# Revit family: RK-ZONE8
name_source: partatom
category: Electrical Equipment
revit_build: Autodesk Revit 2016 (Build: 20150220_1215(x64)
units: mm (PartAtom-declared; Revit-internal decimal feet)

## family parameters
Always vertical = Yes
Cut with Voids When Loaded = No
OmniClass Number = 23.80.30.11.17
OmniClass Title = Distribution Boards and Control Panels
Panel Configuration = Two Columns, Circuits Across
Part Type = Panelboard
Room Calculation Point = No
Round Connector Dimension = Use Diameter
Shared = No
Work Plane-Based = No

## types (1)
- RK-ZONE8
    Access Clearance Bottom = 0 mm  [stored 0 ft]
    Access Clearance Front = 0 mm  [stored 0 ft]
    Access Clearance Left = 0 mm  [stored 0 ft]
    Access Clearance Rear = 0 mm  [stored 0 ft]
    Access Clearance Right = 0 mm  [stored 0 ft]
    Access Clearance Top = 0 mm  [stored 0 ft]
    BMS Links = Yes
    Battery Type = e.g. Alkaline, Lithium Ion Rechargeable
    CE Approval = Number, Yes, No
    Coverage Area = 0.06 m²
    Default elevation = 1219 mm
    Embodied Carbon = kgCO2
    Enclosure Rating = IP rating
    Energy Technology List = External data hyperconnection
    Environmental Product Declaration = 3rd Party Verification
    Expected Life = *Years
    Features = Free text to describe product
    Fire Control Panel Links = Yes
    Frequency = 350 Hz ~ 12 kHz
    Green Guide for Specification = A - E
    Gross Weight = 2.05Kg
    Life Cycle Analysis = A - E
    Location of Manufacturer = Northing,Easting
    Manufacturer Website = External data hyperconnection
    Material = Steel
    Material2 = cutout
    Number of Poles = 3
    O&M Manual = External data hyperconnection
    Overall Height = 165 mm
    Overall Length = 240 mm  [stored 0.787402 ft]
    Overall Width = 225 mm  [stored 0.738189 ft]
    Product Model Number = Or  Code
    Responsible Sourcing of Materials = Endorsing body
    Set Point Concentration = 0 m²
    Supply Phase = 3
    voltage = 100V/70V

note: [stored X ft] marks values corroborated as IEEE doubles in the binary element streams (Revit-internal decimal feet)

## geometry (parser evidence)
native form markers: Sweep x6
no freeform markers — native parametric forms only
